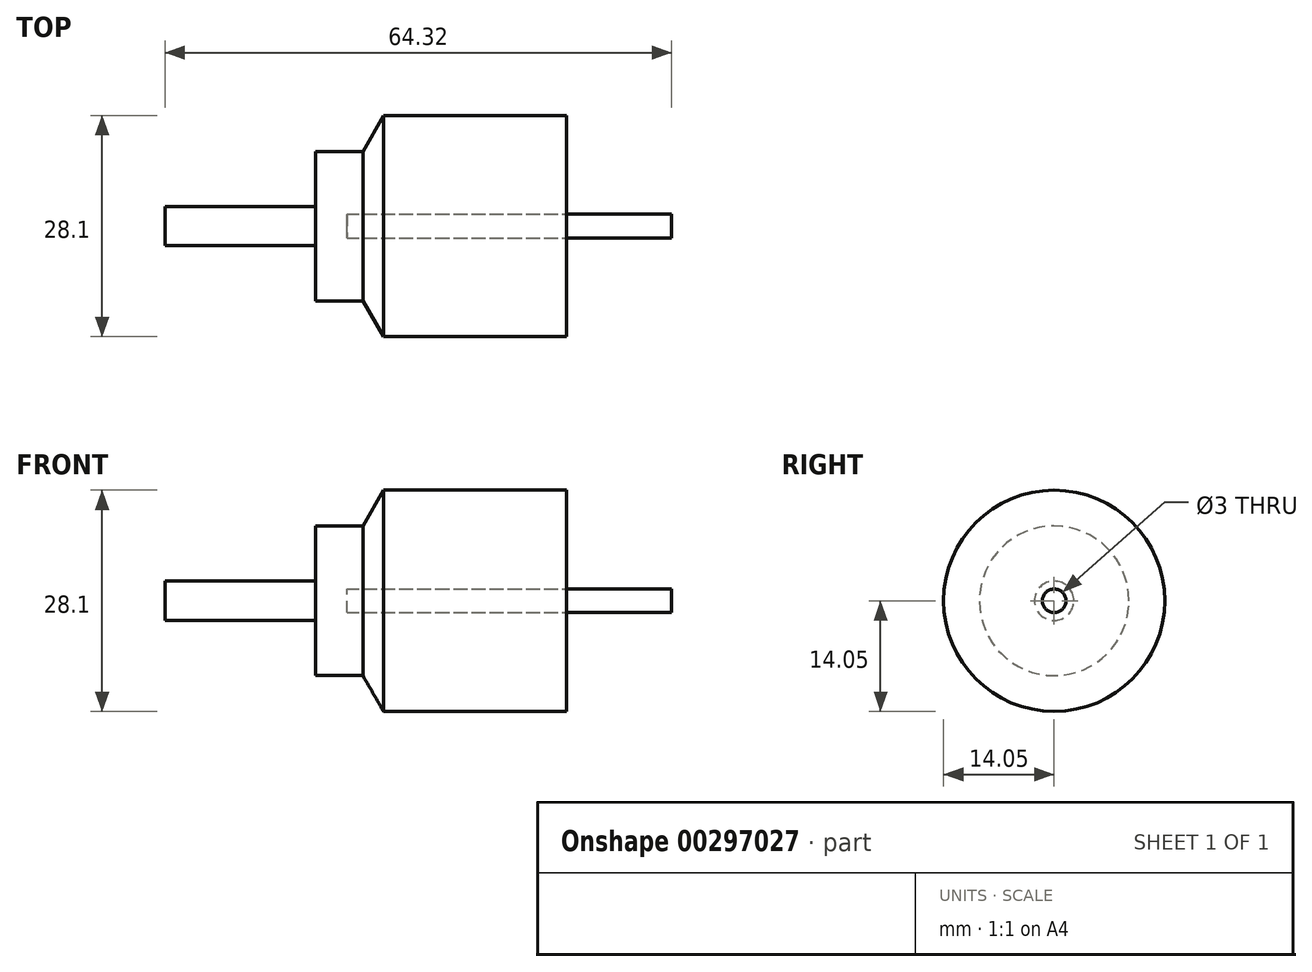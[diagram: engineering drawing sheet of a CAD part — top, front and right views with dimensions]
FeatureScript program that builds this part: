
annotation { "Feature Type Name" : "Feature", "Feature Type Description" : "" }
export const myFeature = defineFeature(function(context is Context, id is Id, definition is map)
    precondition{}
    {
        {
            var Q0;
            Q0=qCreatedBy(makeId("Front.planeOp"),FACE);
            var sketch = newSketch(context, id + "F0", { "sketchPlane" : qUnion([Q0])});
            skLineSegment(sketch, "E0.bottom", {"start": v(-25.9, 14.05) * mm, "end": v(0, 14.05) * mm});
            skLineSegment(sketch, "E0.top", {"start": v(-25.9, -14.05) * mm, "end": v(0, -14.05) * mm});
            skLineSegment(sketch, "E0.left", {"start": v(-25.9, 14.05) * mm, "end": v(-25.9, -14.05) * mm});
            skLineSegment(sketch, "E0.right", {"start": v(0, 14.05) * mm, "end": v(0, -14.05) * mm});
            skLineSegment(sketch, "E1.bottom", {"start": v(-31.9, -9.5) * mm, "end": v(-25.9, -9.5) * mm});
            skLineSegment(sketch, "E1.top", {"start": v(-31.9, 9.5) * mm, "end": v(-25.9, 9.5) * mm});
            skLineSegment(sketch, "E1.left", {"start": v(-31.91, 9.5) * mm, "end": v(-31.91, -9.5) * mm});
            skLineSegment(sketch, "E1.right", {"start": v(-25.9, 9.5) * mm, "end": v(-25.9, -9.5) * mm});
            skLineSegment(sketch, "E2", {"start": v(13.3, 0) * mm, "end": v(-51, 0) * mm});
            skLineSegment(sketch, "E3.bottom", {"start": v(-27.9, 1.5) * mm, "end": v(13.31, 1.5) * mm});
            skLineSegment(sketch, "E3.top", {"start": v(-27.9, -1.5) * mm, "end": v(13.31, -1.5) * mm});
            skLineSegment(sketch, "E3.left", {"start": v(-27.9, 1.5) * mm, "end": v(-27.9, -1.5) * mm});
            skLineSegment(sketch, "E3.right", {"start": v(13.3, 1.5) * mm, "end": v(13.3, -1.5) * mm});
            skPoint(sketch, "E4", {"position": v(13.3, 0) * mm});
            skPoint(sketch, "E5", {"position": v(-31.9, 0) * mm});
            skLineSegment(sketch, "E6.bottom", {"start": v(-51, 2.5) * mm, "end": v(-31.9, 2.5) * mm});
            skLineSegment(sketch, "E6.top", {"start": v(-51, -2.5) * mm, "end": v(-31.9, -2.5) * mm});
            skLineSegment(sketch, "E6.left", {"start": v(-51, 2.5) * mm, "end": v(-51, -2.5) * mm});
            skLineSegment(sketch, "E6.right", {"start": v(-31.91, 2.5) * mm, "end": v(-31.91, -2.5) * mm});
            skLineSegment(sketch, "E7.bottom", {"start": v(0, 1.5) * mm, "end": v(13.3, 1.5) * mm});
            skLineSegment(sketch, "E7.top", {"start": v(0, -1.5) * mm, "end": v(13.3, -1.5) * mm});
            skLineSegment(sketch, "E7.left", {"start": v(0, 1.5) * mm, "end": v(0, -1.5) * mm});
            skLineSegment(sketch, "E8", {"start": v(14.6, 9.5) * mm, "end": v(14.6, -9.5) * mm});
            skPoint(sketch, "E9", {"position": v(14.6, 0) * mm});
            skPoint(sketch, "E10.orphan", {"position": v(0, 0) * mm});
            skLineSegment(sketch, "E11", {"start": v(-25.9, 9.5) * mm, "end": v(-23.27, 14.05) * mm});
            skSolve(sketch);
        }
        {
            var Q0;
            Q0=qCreatedBy(makeId("Front.planeOp"),FACE);
            var sketch = newSketch(context, id + "F1", { "sketchPlane" : qUnion([Q0])});
            skLineSegment(sketch, "E12.0", {"start": v(-25.9, 14.05) * mm, "end": v(0, 14.05) * mm});
            skLineSegment(sketch, "E12.1", {"start": v(-25.9, 14.05) * mm, "end": v(-25.9, -14.05) * mm});
            skLineSegment(sketch, "E12.2", {"start": v(0, 14.05) * mm, "end": v(0, -14.05) * mm});
            skLineSegment(sketch, "E12.3", {"start": v(-25.9, -14.05) * mm, "end": v(0, -14.05) * mm});
            skLineSegment(sketch, "E12.4", {"start": v(13.3, 0) * mm, "end": v(-51, 0) * mm});
            skLineSegment(sketch, "E13.0", {"start": v(0, 1.5) * mm, "end": v(13.3, 1.5) * mm});
            skLineSegment(sketch, "E13.1", {"start": v(0, -1.5) * mm, "end": v(13.3, -1.5) * mm});
            skLineSegment(sketch, "E13.2", {"start": v(13.3, 1.5) * mm, "end": v(13.3, -1.5) * mm});
            skLineSegment(sketch, "E14.0", {"start": v(-27.9, 1.5) * mm, "end": v(13.31, 1.5) * mm});
            skLineSegment(sketch, "E15.0", {"start": v(-25.9, 9.5) * mm, "end": v(-23.27, 14.05) * mm});
            skSolve(sketch);
        }
        {
            var Q0;
            Q0=qCreatedBy(makeId("Front.planeOp"),FACE);
            var sketch = newSketch(context, id + "F2", { "sketchPlane" : qUnion([Q0])});
            skLineSegment(sketch, "E16.0", {"start": v(-27.9, 1.5) * mm, "end": v(-27.9, -1.5) * mm});
            skLineSegment(sketch, "E16.1", {"start": v(-27.9, 1.5) * mm, "end": v(13.31, 1.5) * mm});
            skLineSegment(sketch, "E16.2", {"start": v(13.3, 0) * mm, "end": v(-51, 0) * mm});
            skLineSegment(sketch, "E16.3", {"start": v(-27.9, -1.5) * mm, "end": v(13.31, -1.5) * mm});
            skLineSegment(sketch, "E16.4", {"start": v(13.3, 1.5) * mm, "end": v(13.3, -1.5) * mm});
            skSolve(sketch);
        }
        {
            var Q0;
            Q0=qCreatedBy(makeId("Front.planeOp"),FACE);
            var sketch = newSketch(context, id + "F3", { "sketchPlane" : qUnion([Q0])});
            skLineSegment(sketch, "E17.0", {"start": v(-31.91, 9.5) * mm, "end": v(-31.91, -9.5) * mm});
            skLineSegment(sketch, "E17.1", {"start": v(-51, -2.5) * mm, "end": v(-31.9, -2.5) * mm});
            skLineSegment(sketch, "E17.2", {"start": v(-51, 2.5) * mm, "end": v(-51, -2.5) * mm});
            skLineSegment(sketch, "E17.3", {"start": v(-51, 2.5) * mm, "end": v(-31.9, 2.5) * mm});
            skLineSegment(sketch, "E17.4", {"start": v(13.3, 0) * mm, "end": v(-51, 0) * mm});
            skLineSegment(sketch, "E17.5", {"start": v(-31.9, -9.5) * mm, "end": v(-25.9, -9.5) * mm});
            skLineSegment(sketch, "E17.6", {"start": v(-31.9, 9.5) * mm, "end": v(-25.9, 9.5) * mm});
            skLineSegment(sketch, "E17.7", {"start": v(-25.9, 9.5) * mm, "end": v(-25.9, -9.5) * mm});
            skSolve(sketch);
        }
        {
            var Q0;
            {var subQ0=sQuery(id+"F1.wireOp",EDGE,"E13.0");Q0=makeQuery(id+"F1.imprint","IMPRINT",FACE,{"disambiguationData":[TD([[makeQuery(id+"F1.imprint","IMPRINT",EDGE,{"derivedFrom":subQ0}),-1.0]])]});}
            var Q1;
            {var subQ4=sQuery(id+"F1.wireOp",EDGE,"E15.0");Q1=makeQuery(id+"F1.imprint","IMPRINT",FACE,{"disambiguationData":[TD([[makeQuery(id+"F1.imprint","IMPRINT",EDGE,{"derivedFrom":subQ4}),-1.0]])]});}
            var Q2;
            Q2=sQuery(id+"F1.wireOp",EDGE,"E12.4");
            revolve(context, id + "F4", {"surfaceOperationType" : NewSurfaceOperationType.NEW, "entities" : qUnion([Q0, Q1]), "axis" : qUnion([Q2]), "revolveType" : RevolveType.FULL});
        }
        {
            var Q0;
            {var subQ0=sQuery(id+"F2.wireOp",EDGE,"E16.1");Q0=makeQuery(id+"F2.imprint","IMPRINT",FACE,{"disambiguationData":[TD([[makeQuery(id+"F2.imprint","IMPRINT",EDGE,{"derivedFrom":subQ0}),-1.0]])]});}
            var Q1;
            Q1=sQuery(id+"F2.wireOp",EDGE,"E16.2");
            revolve(context, id + "F5", {"surfaceOperationType" : NewSurfaceOperationType.NEW, "entities" : qUnion([Q0]), "axis" : qUnion([Q1]), "revolveType" : RevolveType.FULL});
        }
        {
            var Q0;
            {var subQ0=sQuery(id+"F3.wireOp",EDGE,"E17.3");Q0=makeQuery(id+"F3.imprint","IMPRINT",FACE,{"disambiguationData":[TD([[makeQuery(id+"F3.imprint","IMPRINT",EDGE,{"derivedFrom":subQ0}),-1.0]])]});}
            var Q1;
            {var subQ5=sQuery(id+"F3.wireOp",EDGE,"E17.6");Q1=makeQuery(id+"F3.imprint","IMPRINT",FACE,{"disambiguationData":[TD([[makeQuery(id+"F3.imprint","IMPRINT",EDGE,{"derivedFrom":subQ5}),-1.0]])]});}
            var Q2;
            Q2=sQuery(id+"F3.wireOp",EDGE,"E17.4");
            revolve(context, id + "F6", {"surfaceOperationType" : NewSurfaceOperationType.NEW, "entities" : qUnion([Q0, Q1]), "axis" : qUnion([Q2]), "revolveType" : RevolveType.FULL});
        }
    });
